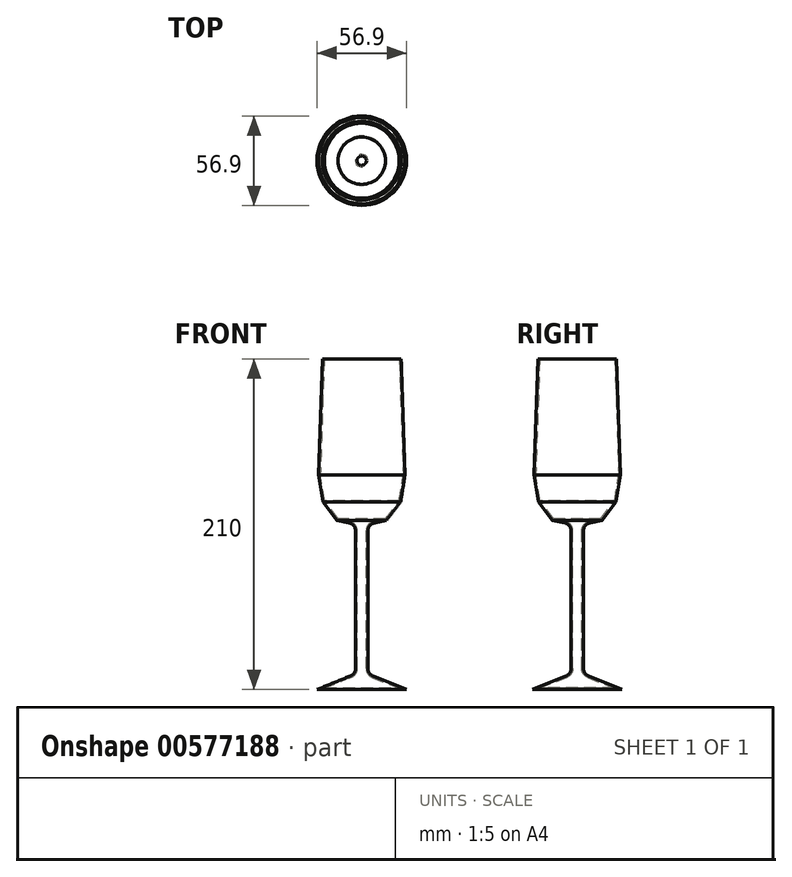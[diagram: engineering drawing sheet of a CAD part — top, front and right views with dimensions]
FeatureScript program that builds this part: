
annotation { "Feature Type Name" : "Feature", "Feature Type Description" : "" }
export const myFeature = defineFeature(function(context is Context, id is Id, definition is map)
    precondition{}
    {
        {
            var Q0;
            Q0=qCreatedBy(makeId("Front.planeOp"),FACE);
            var sketch = newSketch(context, id + "F0", { "sketchPlane" : qUnion([Q0])});
            skLineSegment(sketch, "E0", {"start": v(-25, 117.4) * mm, "end": v(0, 117.4) * mm});
            skLineSegment(sketch, "E1", {"start": v(-27.43, 43.61) * mm, "end": v(-24.73, 26.71) * mm});
            skLineSegment(sketch, "E2", {"start": v(-24.73, 26.71) * mm, "end": v(-15.6, 14.88) * mm});
            skLineSegment(sketch, "E3", {"start": v(-15.6, 14.88) * mm, "end": v(-3.98, 12.4) * mm});
            skLineSegment(sketch, "E4", {"start": v(-3.98, 12.4) * mm, "end": v(-3.93, -82.54) * mm});
            skLineSegment(sketch, "E5", {"start": v(-3.93, -82.54) * mm, "end": v(-28.45, -92.6) * mm});
            skLineSegment(sketch, "E6", {"start": v(-28.45, -92.6) * mm, "end": v(0, -92.6) * mm});
            skLineSegment(sketch, "E7", {"start": v(-25, 117.4) * mm, "end": v(-27.43, 43.61) * mm});
            skLineSegment(sketch, "E8", {"start": v(0, 117.4) * mm, "end": v(0, -92.6) * mm});
            skPoint(sketch, "E9", {"position": v(0, 12.4) * mm});
            skLineSegment(sketch, "E10", {"start": v(0, -92.6) * mm, "end": v(0, -82.6) * mm, "construction": true});
            skSolve(sketch);
        }
        {
            var Q0;
            Q0=makeQuery(id+"F0.imprint","IMPRINT",FACE,{"disambiguationData":[TD([[makeQuery(id+"F0.imprint","IMPRINT",EDGE,{"derivedFrom":sQuery(id+"F0.wireOp",EDGE,"E0")}),-1.0]])]});
            var Q1;
            Q1=sQuery(id+"F0.wireOp",EDGE,"E8");
            revolve(context, id + "F1", {"entities" : qUnion([Q0]), "axis" : qUnion([Q1]), "revolveType" : RevolveType.FULL});
        }
        {
            var Q0;
            Q0=makeQuery(id+"F1.opRevolve","SWEPT_EDGE",EDGE,{"disambiguationData":[OSD([sQuery(id+"F0.wireOp",EDGE,"E4"),sQuery(id+"F0.wireOp",EDGE,"E5")])]});
            var Q1;
            Q1=makeQuery(id+"F1.opRevolve","SWEPT_EDGE",EDGE,{"disambiguationData":[OSD([sQuery(id+"F0.wireOp",EDGE,"E3"),sQuery(id+"F0.wireOp",EDGE,"E4")])]});
            fillet(context, id + "F2", {"entities" : qUnion([Q0, Q1]), "radius" : 5 * mm, "tangentPropagation" : true, "allowEdgeOverflow" : false});
        }
        {
            var Q0;
            Q0=makeQuery(id+"F1.opRevolve","SWEPT_FACE",FACE,{"disambiguationData":[OSD([sQuery(id+"F0.wireOp",EDGE,"E0")])]});
            shell(context, id + "F3", {"entities" : qUnion([Q0]), "thickness" : 1 * mm});
        }
    });
